# Revit family: Trane_TVR_Indoor_2-way Cassette_4TVG0018(24)EF000AA(2nd DC)
name_source: partatom
category: Equipamento mecânico
units: mm (PartAtom-declared; Revit-internal decimal feet)

## family parameters
Com base no plano de trabalho = Não
Compartilhado = Não
Corte com vazios quando carregada = Não
Cota do conector redondo = Utilizar diâmetro
Número OmniClass = 23.75.00.00
Ponto de cálculo do ambiente = Não
Sempre na vertical = Sim
Tipo de parte = Normal
Título OmniClass = Climate Control (HVAC)

## types (2) — shared parameters
Condensation = air
Depth = 591  [stored 1.93898 ft]
Descrição = High efficiency air cooled
Drain pipe = 32  [stored 0.104987 ft]
Fabricante = Trane
Gas = R410a
Gas pipe = 15.9  [stored 0.0521654 ft]
Height = 299
Installation = Indoor installation
Liquid pipe = 9.53
Machine material = grilles：ABS/HIPS
Maximum Fuse Amps = 15 A
Minimum Circuit Amps = 1 A
Net Weight = 35.00 kg
Panel color = SB2014
Power supply = 220-240V, 50/60Hz
URL = https://www.trane.com
Width = 1172  [stored 3.84514 ft]
clearance access behind = 1500
clearance access front = 1500
clearance access left = 100  [stored 0.328084 ft]
clearance access right = 100  [stored 0.328084 ft]

## per-type parameters (varying)
| type | Air Flow | Cooling Capacity | Cooling Power Input | Heating Capacity | Heating Power Input | Series |
| 4TVG0024EF000AA | 1200/1115/1068/1000/921/808/770m3/h | 7 kW | 98 W | 8 kW | 98 W | TVR ULTRA |
| 4TVG0018EF000AA | 980/925/855/800/755/702/670m3/h | 6 kW | 69 W | 6 kW | 69 W | TVR |

note: column(s) folded — value = type name in every type: Modelo

note: [stored X ft] marks values corroborated as IEEE doubles in the binary element streams (Revit-internal decimal feet)

## geometry (parser evidence)
native form markers: Blend x2, Sweep x1
no freeform markers — native parametric forms only
